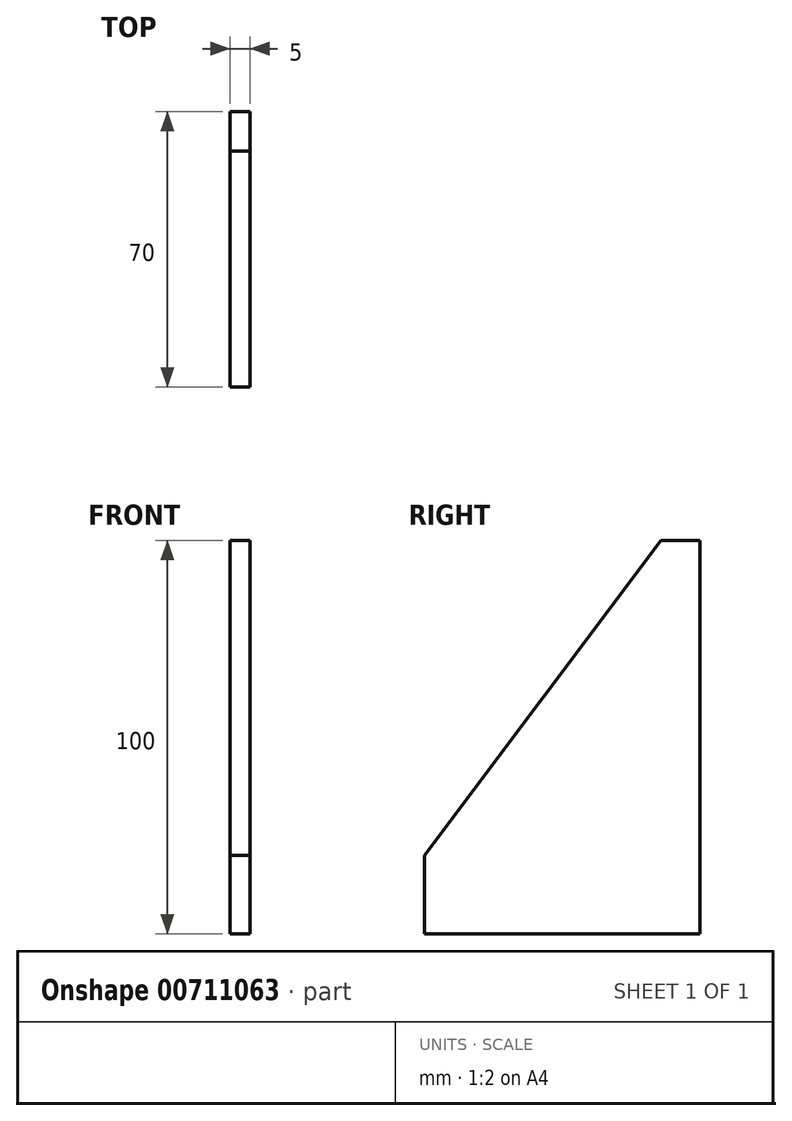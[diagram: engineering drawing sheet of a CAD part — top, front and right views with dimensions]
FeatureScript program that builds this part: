
annotation { "Feature Type Name" : "Feature", "Feature Type Description" : "" }
export const myFeature = defineFeature(function(context is Context, id is Id, definition is map)
    precondition{}
    {
        {
            var Q0;
            Q0=qCreatedBy(makeId("Front.planeOp"),FACE);
            var sketch = newSketch(context, id + "F0", { "sketchPlane" : qUnion([Q0])});
            skLineSegment(sketch, "E0.bottom", {"start": v(0, 0) * mm, "end": v(5, 0) * mm});
            skLineSegment(sketch, "E0.top", {"start": v(0, 100) * mm, "end": v(5, 100) * mm});
            skLineSegment(sketch, "E0.left", {"start": v(0, 0) * mm, "end": v(0, 100) * mm});
            skLineSegment(sketch, "E0.right", {"start": v(5, 0) * mm, "end": v(5, 100) * mm});
            skSolve(sketch);
        }
        {
            var Q0;
            Q0=makeQuery(id+"F0.imprint","IMPRINT",FACE,{"disambiguationData":[TD([[makeQuery(id+"F0.imprint","IMPRINT",EDGE,{"derivedFrom":sQuery(id+"F0.wireOp",EDGE,"E0.bottom")}),1.0]])]});
            extrude(context, id + "F1", {"entities" : qUnion([Q0]), "depth" : 75 * mm, "offsetDistance" : 25.4 * mm});
        }
        {
            var Q0;
            Q0=makeQuery(id+"F1.opExtrude","SWEPT_FACE",FACE,{"disambiguationData":[OSD([sQuery(id+"F0.wireOp",EDGE,"E0.left")])]});
            var sketch = newSketch(context, id + "F2", { "sketchPlane" : qUnion([Q0])});
            skLineSegment(sketch, "E1", {"start": v(0, 100) * mm, "end": v(15, 100) * mm});
            skLineSegment(sketch, "E2", {"start": v(75, 0) * mm, "end": v(75, 20) * mm});
            skLineSegment(sketch, "E3", {"start": v(75, 20) * mm, "end": v(15, 100) * mm});
            skSolve(sketch);
        }
        {
            var Q0;
            {var subQ0=sQuery(id+"F2.wireOp",EDGE,"E3");Q0=makeQuery(id+"F2.imprint","IMPRINT",FACE,{"disambiguationData":[TD([[makeQuery(id+"F2.imprint","IMPRINT",EDGE,{"derivedFrom":subQ0}),-1.0]])]});}
            extrude(context, id + "F3", {"entities" : qUnion([Q0]), "operationType" : NewBodyOperationType.REMOVE, "oppositeDirection" : true, "depth" : 5 * mm, "offsetDistance" : 25.4 * mm});
        }
        {
            var Q0;
            Q0=makeQuery(id+"F1.opExtrude","CAP_FACE",FACE,{"disambiguationData":[OSD([sQuery(id+"F0.wireOp",EDGE,"E0.bottom"),sQuery(id+"F0.wireOp",EDGE,"E0.top"),sQuery(id+"F0.wireOp",EDGE,"E0.left"),sQuery(id+"F0.wireOp",EDGE,"E0.right")])],"isStart":true});
            extrude(context, id + "F4", {"entities" : qUnion([Q0]), "operationType" : NewBodyOperationType.REMOVE, "oppositeDirection" : true, "depth" : 5 * mm, "offsetDistance" : 25.4 * mm});
        }
    });
